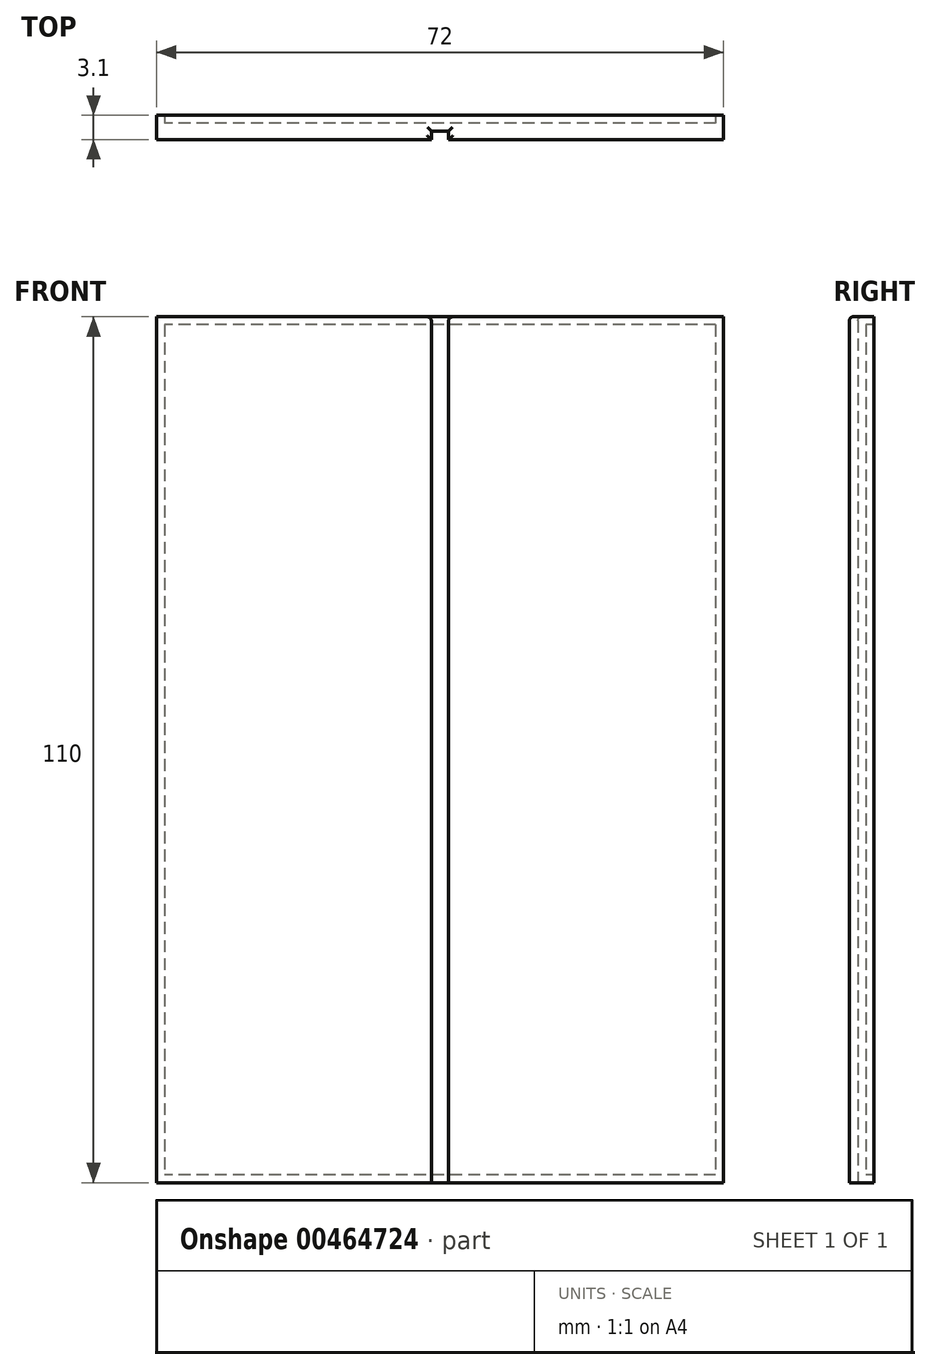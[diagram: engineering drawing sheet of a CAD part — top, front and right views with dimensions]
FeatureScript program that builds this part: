
annotation { "Feature Type Name" : "Feature", "Feature Type Description" : "" }
export const myFeature = defineFeature(function(context is Context, id is Id, definition is map)
    precondition{}
    {
        {
            var Q0;
            Q0=qCreatedBy(makeId("Top.planeOp"),FACE);
            var sketch = newSketch(context, id + "F0", { "sketchPlane" : qUnion([Q0])});
            skLineSegment(sketch, "E0.bottom", {"start": v(-7.52, 0) * mm, "end": v(64.48, 0) * mm});
            skLineSegment(sketch, "E0.top", {"start": v(-7.52, -1) * mm, "end": v(64.48, -1) * mm});
            skLineSegment(sketch, "E0.left", {"start": v(-7.52, 0) * mm, "end": v(-7.52, -1) * mm});
            skLineSegment(sketch, "E0.right", {"start": v(64.48, 0) * mm, "end": v(64.48, -1) * mm});
            skLineSegment(sketch, "E1.bottom", {"start": v(-7.52, -1) * mm, "end": v(27.38, -1) * mm});
            skLineSegment(sketch, "E1.top", {"start": v(-7.52, -2.1) * mm, "end": v(27.38, -2.1) * mm});
            skLineSegment(sketch, "E1.left", {"start": v(-7.52, -1) * mm, "end": v(-7.52, -2.1) * mm});
            skLineSegment(sketch, "E1.right", {"start": v(27.38, -1) * mm, "end": v(27.38, -2.1) * mm});
            skLineSegment(sketch, "E2.bottom", {"start": v(64.48, -1) * mm, "end": v(29.58, -1) * mm});
            skLineSegment(sketch, "E2.top", {"start": v(64.48, -2.1) * mm, "end": v(29.58, -2.1) * mm});
            skLineSegment(sketch, "E2.left", {"start": v(64.48, -1) * mm, "end": v(64.48, -2.1) * mm});
            skLineSegment(sketch, "E2.right", {"start": v(29.58, -1) * mm, "end": v(29.58, -2.1) * mm});
            skSolve(sketch);
        }
        {
            var Q0;
            Q0 = qSketchRegion(id + "F0", true);
            extrude(context, id + "F1", {"entities" : qUnion([Q0]), "depth" : 110 * mm});
        }
        {
            var Q0;
            Q0=makeQuery(id+"F1.opExtrude","SWEPT_FACE",FACE,{"disambiguationData":[OSD([sQuery(id+"F0.wireOp",EDGE,"E0.bottom")])]});
            var sketch = newSketch(context, id + "F2", { "sketchPlane" : qUnion([Q0])});
            skLineSegment(sketch, "E3.bottom", {"start": v(7.52, 110) * mm, "end": v(6.52, 110) * mm});
            skLineSegment(sketch, "E3.top", {"start": v(7.52, 0) * mm, "end": v(6.52, 0) * mm});
            skLineSegment(sketch, "E3.left", {"start": v(7.52, 110) * mm, "end": v(7.52, 0) * mm});
            skLineSegment(sketch, "E3.right", {"start": v(6.52, 110) * mm, "end": v(6.52, 0) * mm});
            skLineSegment(sketch, "E4.bottom", {"start": v(-64.48, 110) * mm, "end": v(-63.48, 110) * mm});
            skLineSegment(sketch, "E4.top", {"start": v(-64.48, 0) * mm, "end": v(-63.48, 0) * mm});
            skLineSegment(sketch, "E4.left", {"start": v(-64.48, 110) * mm, "end": v(-64.48, 0) * mm});
            skLineSegment(sketch, "E4.right", {"start": v(-63.48, 110) * mm, "end": v(-63.48, 0) * mm});
            skLineSegment(sketch, "E5.bottom", {"start": v(-63.48, 110) * mm, "end": v(6.52, 110) * mm});
            skLineSegment(sketch, "E5.top", {"start": v(-63.48, 109) * mm, "end": v(6.52, 109) * mm});
            skLineSegment(sketch, "E5.left", {"start": v(-63.48, 110) * mm, "end": v(-63.48, 109) * mm});
            skLineSegment(sketch, "E5.right", {"start": v(6.52, 110) * mm, "end": v(6.52, 109) * mm});
            skLineSegment(sketch, "E6.bottom", {"start": v(-63.48, 0) * mm, "end": v(6.52, 0) * mm});
            skLineSegment(sketch, "E6.top", {"start": v(-63.48, 1) * mm, "end": v(6.52, 1) * mm});
            skLineSegment(sketch, "E6.left", {"start": v(-63.48, 0) * mm, "end": v(-63.48, 1) * mm});
            skLineSegment(sketch, "E6.right", {"start": v(6.52, 0) * mm, "end": v(6.52, 1) * mm});
            skSolve(sketch);
        }
        {
            var Q0;
            Q0 = qSketchRegion(id + "F2", true);
            extrude(context, id + "F3", {"entities" : qUnion([Q0]), "operationType" : NewBodyOperationType.ADD, "depth" : 1 * mm});
        }
        {
            var Q0;
            Q0=makeQuery(id+"F1.opExtrude","CAP_EDGE",EDGE,{"disambiguationData":[OSD([sQuery(id+"F0.wireOp",EDGE,"E1.top")])],"isStart":false});
            var Q1;
            Q1=makeQuery(id+"F1.opExtrude","CAP_EDGE",EDGE,{"disambiguationData":[OSD([sQuery(id+"F0.wireOp",EDGE,"E2.right")])],"isStart":false});
            var Q2;
            Q2=makeQuery(id+"F1.opExtrude","CAP_EDGE",EDGE,{"disambiguationData":[OSD([sQuery(id+"F0.wireOp",EDGE,"E1.right")])],"isStart":false});
            var Q3;
            Q3=makeQuery(id+"F1.opExtrude","CAP_EDGE",EDGE,{"disambiguationData":[OSD([sQuery(id+"F0.wireOp",EDGE,"E0.top")])],"isStart":false});
            var Q4;
            Q4=makeQuery(id+"F1.opExtrude","CAP_EDGE",EDGE,{"disambiguationData":[OSD([sQuery(id+"F0.wireOp",EDGE,"E2.top")])],"isStart":false});
            fillet(context, id + "F4", {"entities" : qUnion([Q0, Q1, Q2, Q3, Q4]), "radius" : .5 * mm, "tangentPropagation" : true, "allowEdgeOverflow" : false});
        }
    });
